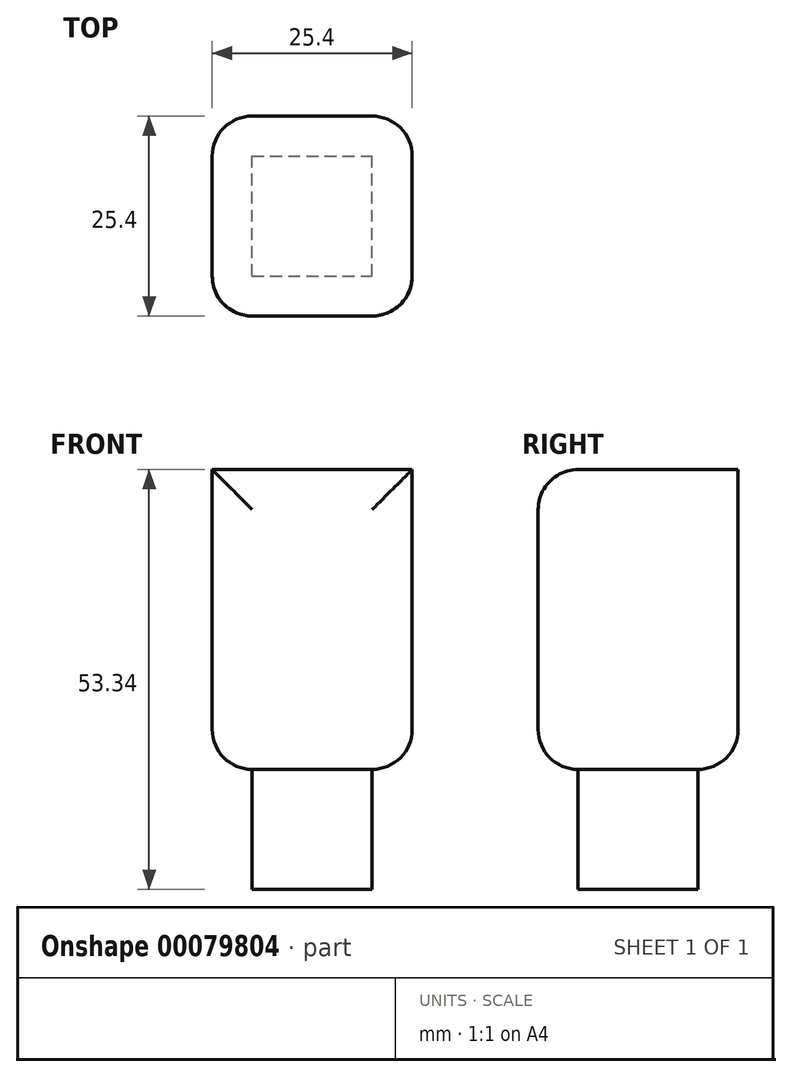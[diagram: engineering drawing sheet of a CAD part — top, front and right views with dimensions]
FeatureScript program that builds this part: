
annotation { "Feature Type Name" : "Feature", "Feature Type Description" : "" }
export const myFeature = defineFeature(function(context is Context, id is Id, definition is map)
    precondition{}
    {
        {
            var Q0;
            Q0=qCreatedBy(makeId("Top.planeOp"),FACE);
            var sketch = newSketch(context, id + "F0", { "sketchPlane" : qUnion([Q0])});
            skLineSegment(sketch, "E0.bottom", {"start": v(-12.7, -12.7) * mm, "end": v(12.7, -12.7) * mm});
            skLineSegment(sketch, "E0.top", {"start": v(-12.7, 12.7) * mm, "end": v(12.7, 12.7) * mm});
            skLineSegment(sketch, "E0.left", {"start": v(-12.7, -12.7) * mm, "end": v(-12.7, 12.7) * mm});
            skLineSegment(sketch, "E0.right", {"start": v(12.7, -12.7) * mm, "end": v(12.7, 12.7) * mm});
            skPoint(sketch, "E0.middle", {"position": v(0, 0) * mm});
            skSolve(sketch);
        }
        {
            var Q0;
            Q0=makeQuery(id+"F0.imprint","IMPRINT",FACE,{"disambiguationData":[TD([[makeQuery(id+"F0.imprint","IMPRINT",EDGE,{"derivedFrom":sQuery(id+"F0.wireOp",EDGE,"E0.bottom")}),1.0]])]});
            extrude(context, id + "F1", {"entities" : qUnion([Q0]), "oppositeDirection" : true, "depth" : 38.1 * mm});
        }
        {
            var Q0;
            Q0=makeQuery(id+"F1.opExtrude","CAP_EDGE",EDGE,{"disambiguationData":[OSD([sQuery(id+"F0.wireOp",EDGE,"E0.left")])],"isStart":false});
            fillet(context, id + "F2", {"entities" : qUnion([Q0]), "radius" : 5.08 * mm, "tangentPropagation" : true, "allowEdgeOverflow" : false});
        }
        {
            var Q0;
            Q0=makeQuery(id+"F1.opExtrude","CAP_FACE",FACE,{"disambiguationData":[OSD([sQuery(id+"F0.wireOp",EDGE,"E0.bottom"),sQuery(id+"F0.wireOp",EDGE,"E0.top"),sQuery(id+"F0.wireOp",EDGE,"E0.left"),sQuery(id+"F0.wireOp",EDGE,"E0.right")])],"isStart":false});
            var Q1;
            Q1=makeQuery(id+"F1.opExtrude","SWEPT_FACE",FACE,{"disambiguationData":[OSD([sQuery(id+"F0.wireOp",EDGE,"E0.bottom")])]});
            var Q2;
            Q2=makeQuery(id+"F1.opExtrude","SWEPT_EDGE",EDGE,{"disambiguationData":[OSD([sQuery(id+"F0.wireOp",EDGE,"E0.top"),sQuery(id+"F0.wireOp",EDGE,"E0.right")])]});
            fillet(context, id + "F3", {"entities" : qUnion([Q0, Q1, Q2]), "radius" : 5.08 * mm, "tangentPropagation" : true, "allowEdgeOverflow" : false});
        }
        {
            var Q0;
            Q0=makeQuery(id+"F1.opExtrude","CAP_FACE",FACE,{"disambiguationData":[OSD([sQuery(id+"F0.wireOp",EDGE,"E0.bottom"),sQuery(id+"F0.wireOp",EDGE,"E0.top"),sQuery(id+"F0.wireOp",EDGE,"E0.left"),sQuery(id+"F0.wireOp",EDGE,"E0.right")])],"isStart":false});
            extrude(context, id + "F4", {"entities" : qUnion([Q0]), "operationType" : NewBodyOperationType.ADD, "depth" : 15.24 * mm});
        }
    });
